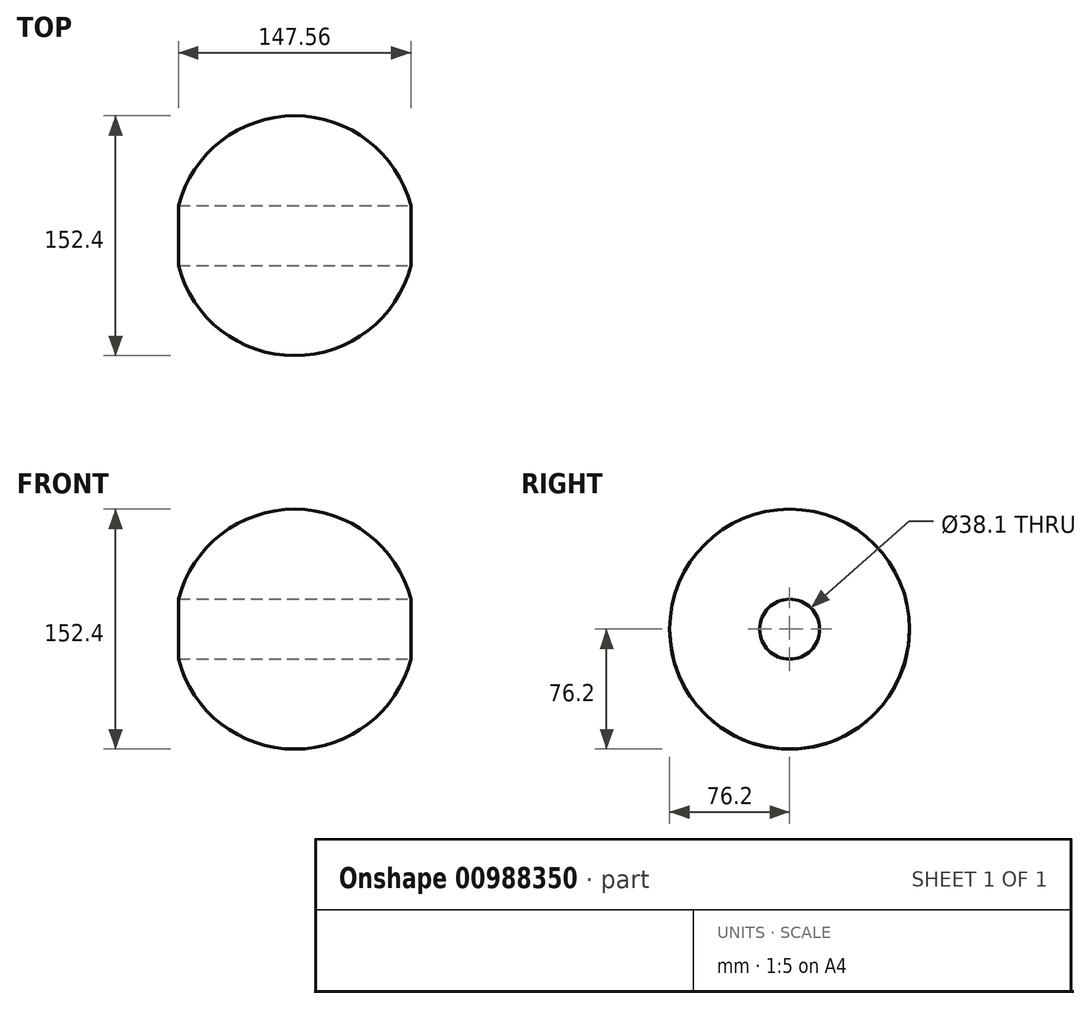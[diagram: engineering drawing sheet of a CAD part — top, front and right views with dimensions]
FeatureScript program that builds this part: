
annotation { "Feature Type Name" : "Feature", "Feature Type Description" : "" }
export const myFeature = defineFeature(function(context is Context, id is Id, definition is map)
    precondition{}
    {
        {
            var Q0;
            Q0=qCreatedBy(makeId("Top.planeOp"),FACE);
            var sketch = newSketch(context, id + "F0", { "sketchPlane" : qUnion([Q0])});
            skArc(sketch, "E0", {"start": v(0, 76.2) * mm, "mid": v(76.2, 0) * mm, "end": v(0, -76.2) * mm});
            skLineSegment(sketch, "E1", {"start": v(0, 76.2) * mm, "end": v(0, -76.2) * mm});
            skSolve(sketch);
        }
        {
            var Q0;
            Q0 = qSketchRegion(id + "F0", true);
            var Q1;
            Q1=sQuery(id+"F0.wireOp",EDGE,"E1");
            revolve(context, id + "F1", {"surfaceOperationType" : NewSurfaceOperationType.NEW, "entities" : qUnion([Q0]), "axis" : qUnion([Q1]), "revolveType" : RevolveType.FULL});
        }
        {
            var Q0;
            Q0=qCreatedBy(makeId("Right.planeOp"),FACE);
            var sketch = newSketch(context, id + "F2", { "sketchPlane" : qUnion([Q0])});
            skCircle(sketch, "E2", {"center": v(0, 0) * mm, "radius": 19.05 * mm});
            skSolve(sketch);
        }
        {
            var Q0;
            Q0 = qSketchRegion(id + "F2", true);
            extrude(context, id + "F3", {"entities" : qUnion([Q0]), "operationType" : NewBodyOperationType.REMOVE, "endBound" : BoundingType.THROUGH_ALL, "oppositeDirection" : true, "depth" : 25.4 * mm, "offsetDistance" : 25.4 * mm, "hasSecondDirection" : true, "secondDirectionBound" : SecondDirectionBoundingType.THROUGH_ALL, "secondDirectionOppositeDirection" : false, "secondDirectionDepth" : 25.4 * mm});
        }
    });
